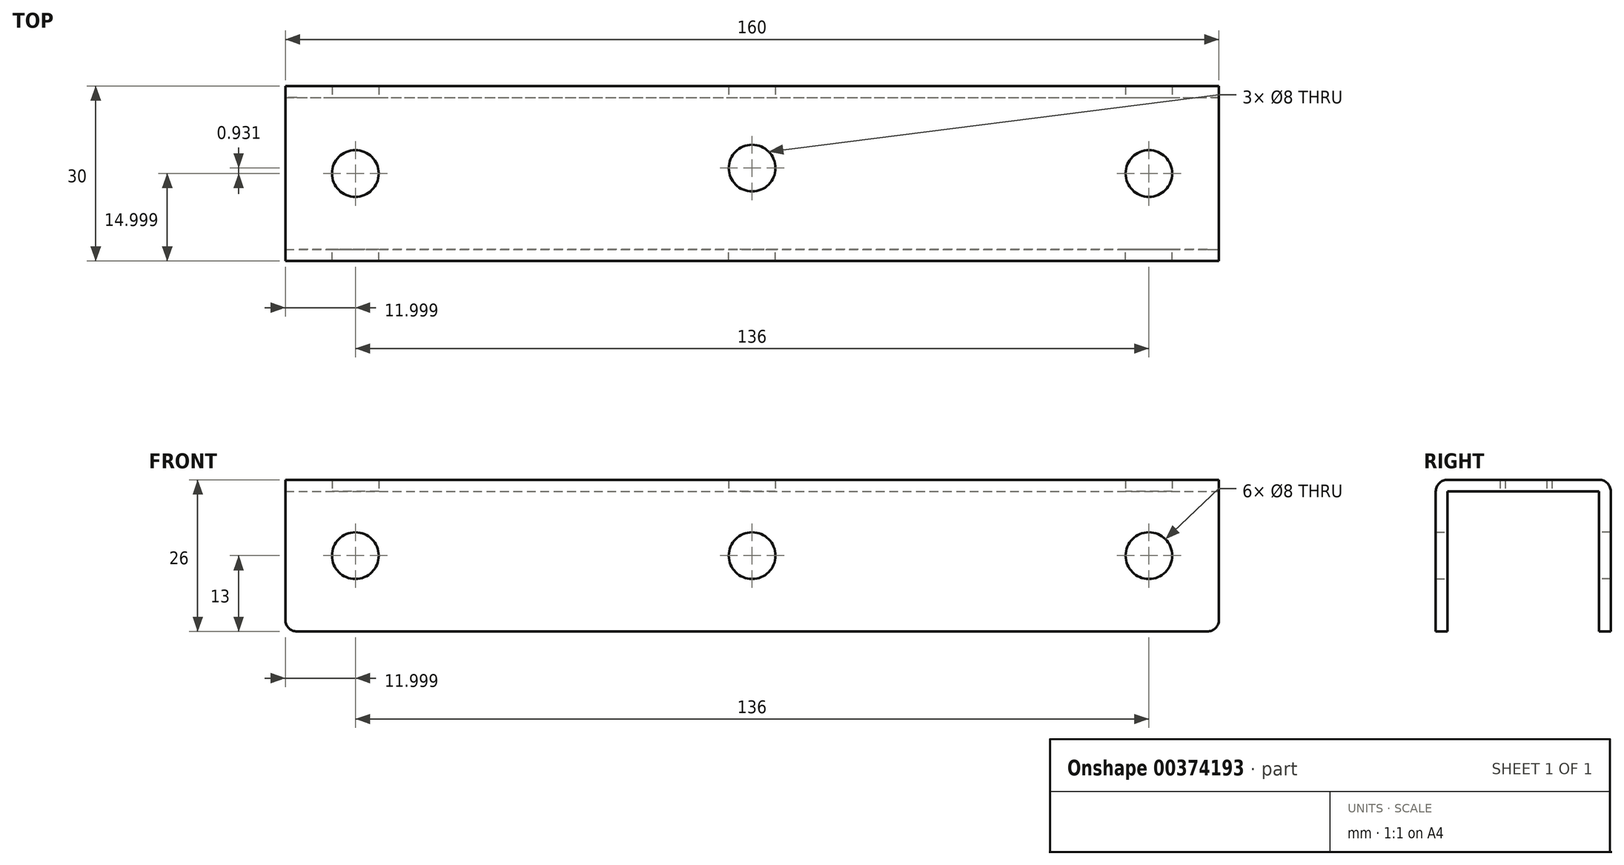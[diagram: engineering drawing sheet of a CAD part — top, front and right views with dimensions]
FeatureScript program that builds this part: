
annotation { "Feature Type Name" : "Feature", "Feature Type Description" : "" }
export const myFeature = defineFeature(function(context is Context, id is Id, definition is map)
    precondition{}
    {
        {
            var Q0;
            Q0=qCreatedBy(makeId("Top.planeOp"),FACE);
            var sketch = newSketch(context, id + "F0", { "sketchPlane" : qUnion([Q0])});
            skLineSegment(sketch, "E0.bottom", {"start": v(-78.8, -7.38) * mm, "end": v(81.2, -7.38) * mm});
            skLineSegment(sketch, "E0.top", {"start": v(-78.8, -33.38) * mm, "end": v(81.2, -33.38) * mm});
            skLineSegment(sketch, "E0.left", {"start": v(-78.8, -7.38) * mm, "end": v(-78.8, -33.38) * mm});
            skLineSegment(sketch, "E0.right", {"start": v(81.2, -7.38) * mm, "end": v(81.2, -33.38) * mm});
            skLineSegment(sketch, "E1", {"start": v(-66.8, -7.38) * mm, "end": v(-66.8, -33.38) * mm, "construction": true});
            skLineSegment(sketch, "E2", {"start": v(69.2, -7.38) * mm, "end": v(69.2, -33.38) * mm, "construction": true});
            skLineSegment(sketch, "E3", {"start": v(1.2, -5.52) * mm, "end": v(1.2, -33.38) * mm, "construction": true});
            skCircle(sketch, "E4", {"center": v(1.2, -19.45) * mm, "radius": 4 * mm});
            skCircle(sketch, "E5", {"center": v(69.2, -20.38) * mm, "radius": 4 * mm});
            skCircle(sketch, "E6", {"center": v(-66.8, -20.38) * mm, "radius": 4 * mm});
            skSolve(sketch);
        }
        {
            var Q0;
            Q0=makeQuery(id+"F0.imprint","IMPRINT",FACE,{"disambiguationData":[TD([[makeQuery(id+"F0.imprint","IMPRINT",EDGE,{"derivedFrom":sQuery(id+"F0.wireOp",EDGE,"E0.bottom")}),-1.0]])]});
            extrude(context, id + "F1", {"entities" : qUnion([Q0]), "depth" : 2 * mm});
        }
        {
            var Q0;
            Q0=qCreatedBy(makeId("Front.planeOp"),FACE);
            var sketch = newSketch(context, id + "F2", { "sketchPlane" : qUnion([Q0])});
            skLineSegment(sketch, "E7.0", {"start": v(-78.8, 2) * mm, "end": v(81.2, 2) * mm});
            skLineSegment(sketch, "E8", {"start": v(81.2, -24) * mm, "end": v(81.2, 2) * mm});
            skLineSegment(sketch, "E9", {"start": v(-78.8, 2) * mm, "end": v(-78.8, -24) * mm});
            skLineSegment(sketch, "E10", {"start": v(-78.8, -24) * mm, "end": v(81.2, -24) * mm});
            skLineSegment(sketch, "E11", {"start": v(69.2, 2) * mm, "end": v(69.2, -24) * mm, "construction": true});
            skLineSegment(sketch, "E12", {"start": v(-66.8, 2) * mm, "end": v(-66.8, -24) * mm, "construction": true});
            skLineSegment(sketch, "E13", {"start": v(1.2, 2) * mm, "end": v(1.2, -24) * mm, "construction": true});
            skCircle(sketch, "E14", {"center": v(1.2, -11) * mm, "radius": 4 * mm});
            skCircle(sketch, "E15", {"center": v(-66.8, -11) * mm, "radius": 4 * mm});
            skCircle(sketch, "E16", {"center": v(69.2, -11) * mm, "radius": 4 * mm});
            skSolve(sketch);
        }
        {
            var Q0;
            Q0=makeQuery(id+"F1.opExtrude","SWEPT_FACE",FACE,{"disambiguationData":[OSD([sQuery(id+"F0.wireOp",EDGE,"E0.bottom")])]});
            cPlane(context, id + "F3", {"entities" : qUnion([Q0]), "cplaneType" : CPlaneType.OFFSET, "offset" : 0 * mm, "width" : 150 * mm, "height" : 150 * mm});
        }
        {
            var Q0;
            Q0=qCreatedBy(id+"F3.planeOp",FACE);
            var sketch = newSketch(context, id + "F4", { "sketchPlane" : qUnion([Q0])});
            skLineSegment(sketch, "E17.0.0", {"start": v(78.8, 2) * mm, "end": v(78.8, -24) * mm});
            skLineSegment(sketch, "E17.0.1", {"start": v(78.8, -24) * mm, "end": v(-81.2, -24) * mm});
            skLineSegment(sketch, "E17.0.2", {"start": v(-81.2, -24) * mm, "end": v(-81.2, 2) * mm});
            skLineSegment(sketch, "E17.0.3", {"start": v(-81.2, 2) * mm, "end": v(78.8, 2) * mm});
            skCircle(sketch, "E18.0", {"center": v(-69.2, -11) * mm, "radius": 4 * mm});
            skCircle(sketch, "E19.0", {"center": v(-1.2, -11) * mm, "radius": 4 * mm});
            skCircle(sketch, "E20.0", {"center": v(66.8, -11) * mm, "radius": 4 * mm});
            skSolve(sketch);
        }
        {
            var Q0;
            Q0=makeQuery(id+"F1.opExtrude","SWEPT_FACE",FACE,{"disambiguationData":[OSD([sQuery(id+"F0.wireOp",EDGE,"E0.top")])]});
            cPlane(context, id + "F5", {"entities" : qUnion([Q0]), "cplaneType" : CPlaneType.OFFSET, "offset" : 0 * mm, "width" : 150 * mm, "height" : 150 * mm});
        }
        {
            var Q0;
            Q0=qCreatedBy(id+"F5.planeOp",FACE);
            var sketch = newSketch(context, id + "F6", { "sketchPlane" : qUnion([Q0])});
            skLineSegment(sketch, "E21.0.0", {"start": v(-78.8, 2) * mm, "end": v(81.2, 2) * mm});
            skLineSegment(sketch, "E21.0.1", {"start": v(81.2, 2) * mm, "end": v(81.2, -24) * mm});
            skLineSegment(sketch, "E21.0.2", {"start": v(81.2, -24) * mm, "end": v(-78.8, -24) * mm});
            skLineSegment(sketch, "E21.0.3", {"start": v(-78.8, -24) * mm, "end": v(-78.8, 2) * mm});
            skCircle(sketch, "E22.0", {"center": v(-66.8, -11) * mm, "radius": 4 * mm});
            skCircle(sketch, "E23.0", {"center": v(1.2, -11) * mm, "radius": 4 * mm});
            skCircle(sketch, "E24.0.0", {"center": v(69.2, -11) * mm, "radius": 4 * mm});
            skSolve(sketch);
        }
        {
            var Q0;
            Q0=makeQuery(id+"F4.imprint","IMPRINT",FACE,{"disambiguationData":[TD([[makeQuery(id+"F4.imprint","IMPRINT",EDGE,{"derivedFrom":sQuery(id+"F4.wireOp",EDGE,"E17.0.0")}),-1.0]])]});
            extrude(context, id + "F7", {"entities" : qUnion([Q0]), "operationType" : NewBodyOperationType.ADD, "depth" : 2 * mm});
        }
        {
            var Q0;
            Q0=makeQuery(id+"F6.imprint","IMPRINT",FACE,{"disambiguationData":[TD([[makeQuery(id+"F6.imprint","IMPRINT",EDGE,{"derivedFrom":sQuery(id+"F6.wireOp",EDGE,"E21.0.0")}),-1.0]])]});
            extrude(context, id + "F8", {"entities" : qUnion([Q0]), "operationType" : NewBodyOperationType.ADD, "depth" : 2 * mm});
        }
        {
            var Q0;
            Q0=makeQuery(id+"F7.opExtrude","CAP_EDGE",EDGE,{"disambiguationData":[OSD([sQuery(id+"F4.wireOp",EDGE,"E17.0.3")])],"isStart":false});
            var Q1;
            Q1=makeQuery(id+"F8.opExtrude","CAP_EDGE",EDGE,{"disambiguationData":[OSD([sQuery(id+"F6.wireOp",EDGE,"E21.0.0")])],"isStart":false});
            var Q2;
            Q2=makeQuery(id+"F8.opExtrude","SWEPT_EDGE",EDGE,{"disambiguationData":[OSD([sQuery(id+"F6.wireOp",EDGE,"E21.0.2"),sQuery(id+"F6.wireOp",EDGE,"E21.0.3")])]});
            var Q3;
            Q3=makeQuery(id+"F7.opExtrude","SWEPT_EDGE",EDGE,{"disambiguationData":[OSD([sQuery(id+"F4.wireOp",EDGE,"E17.0.0"),sQuery(id+"F4.wireOp",EDGE,"E17.0.1")])]});
            var Q4;
            Q4=makeQuery(id+"F8.opExtrude","SWEPT_EDGE",EDGE,{"disambiguationData":[OSD([sQuery(id+"F6.wireOp",EDGE,"E21.0.1"),sQuery(id+"F6.wireOp",EDGE,"E21.0.2")])]});
            var Q5;
            Q5=makeQuery(id+"F7.opExtrude","SWEPT_EDGE",EDGE,{"disambiguationData":[OSD([sQuery(id+"F4.wireOp",EDGE,"E17.0.1"),sQuery(id+"F4.wireOp",EDGE,"E17.0.2")])]});
            fillet(context, id + "F9", {"entities" : qUnion([Q0, Q1, Q2, Q3, Q4, Q5]), "radius" : 2 * mm, "tangentPropagation" : true, "allowEdgeOverflow" : false});
        }
    });
